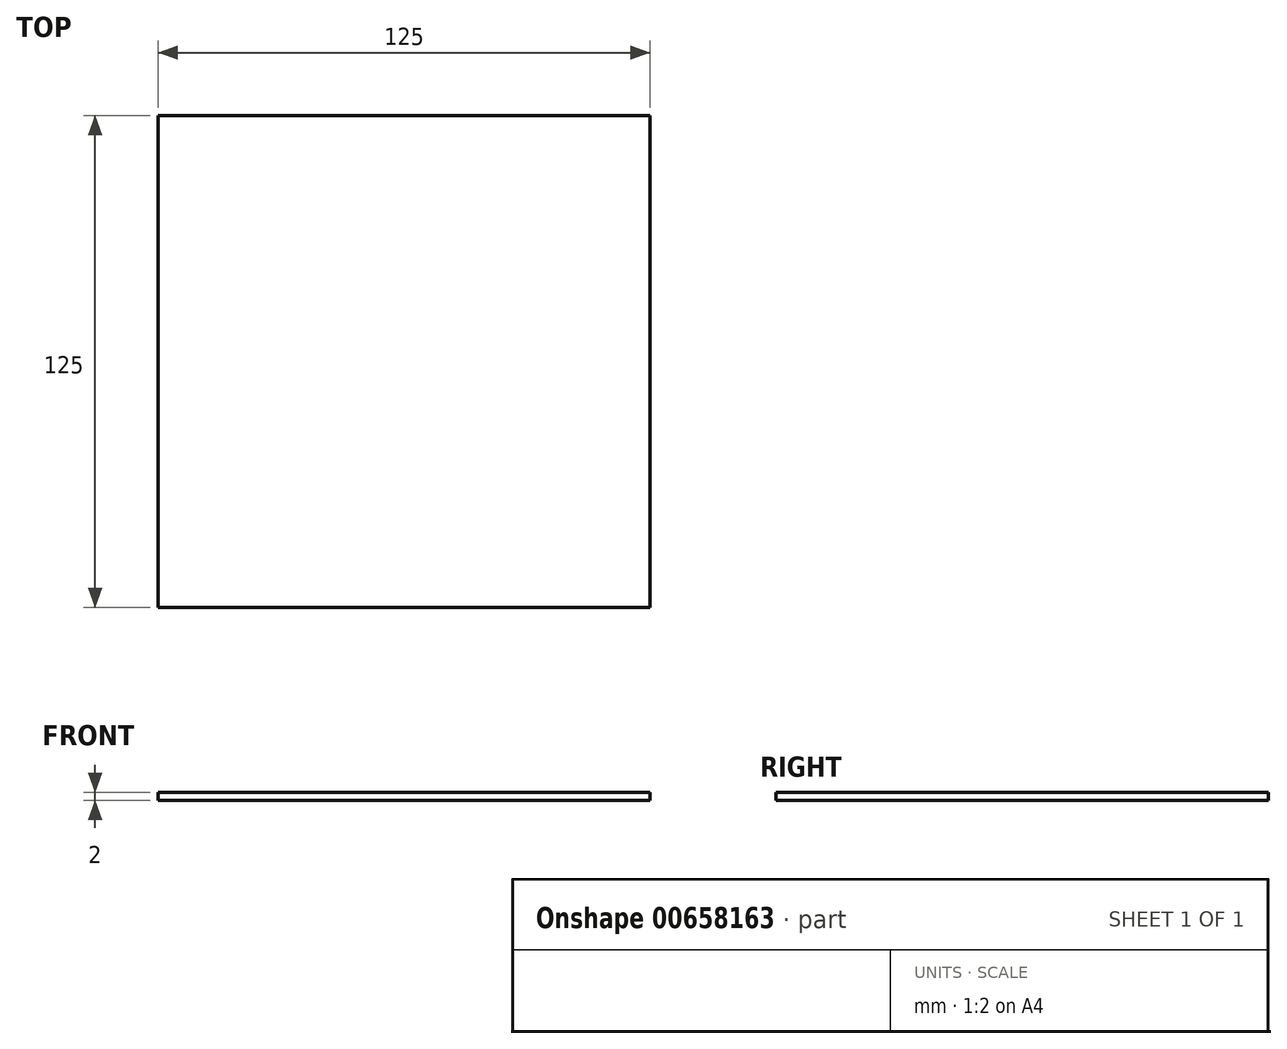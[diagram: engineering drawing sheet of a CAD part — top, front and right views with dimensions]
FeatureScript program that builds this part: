
annotation { "Feature Type Name" : "Feature", "Feature Type Description" : "" }
export const myFeature = defineFeature(function(context is Context, id is Id, definition is map)
    precondition{}
    {
        {
            var Q0;
            Q0=qCreatedBy(makeId("Top.planeOp"),FACE);
            var sketch = newSketch(context, id + "F0", { "sketchPlane" : qUnion([Q0])});
            skLineSegment(sketch, "E0.bottom", {"start": v(-63.98, 61.8) * mm, "end": v(61.02, 61.8) * mm});
            skLineSegment(sketch, "E0.top", {"start": v(-63.98, -63.2) * mm, "end": v(61.02, -63.2) * mm});
            skLineSegment(sketch, "E0.left", {"start": v(-63.98, 61.8) * mm, "end": v(-63.98, -63.2) * mm});
            skLineSegment(sketch, "E0.right", {"start": v(61.02, 61.8) * mm, "end": v(61.02, -63.2) * mm});
            skSolve(sketch);
        }
        {
            var Q0;
            Q0=makeQuery(id+"F0.imprint","IMPRINT",FACE,{"disambiguationData":[TD([[makeQuery(id+"F0.imprint","IMPRINT",EDGE,{"derivedFrom":sQuery(id+"F0.wireOp",EDGE,"E0.bottom")}),-1.0]])]});
            extrude(context, id + "F1", {"entities" : qUnion([Q0]), "depth" : 2 * mm, "offsetDistance" : 25 * mm});
        }
    });
